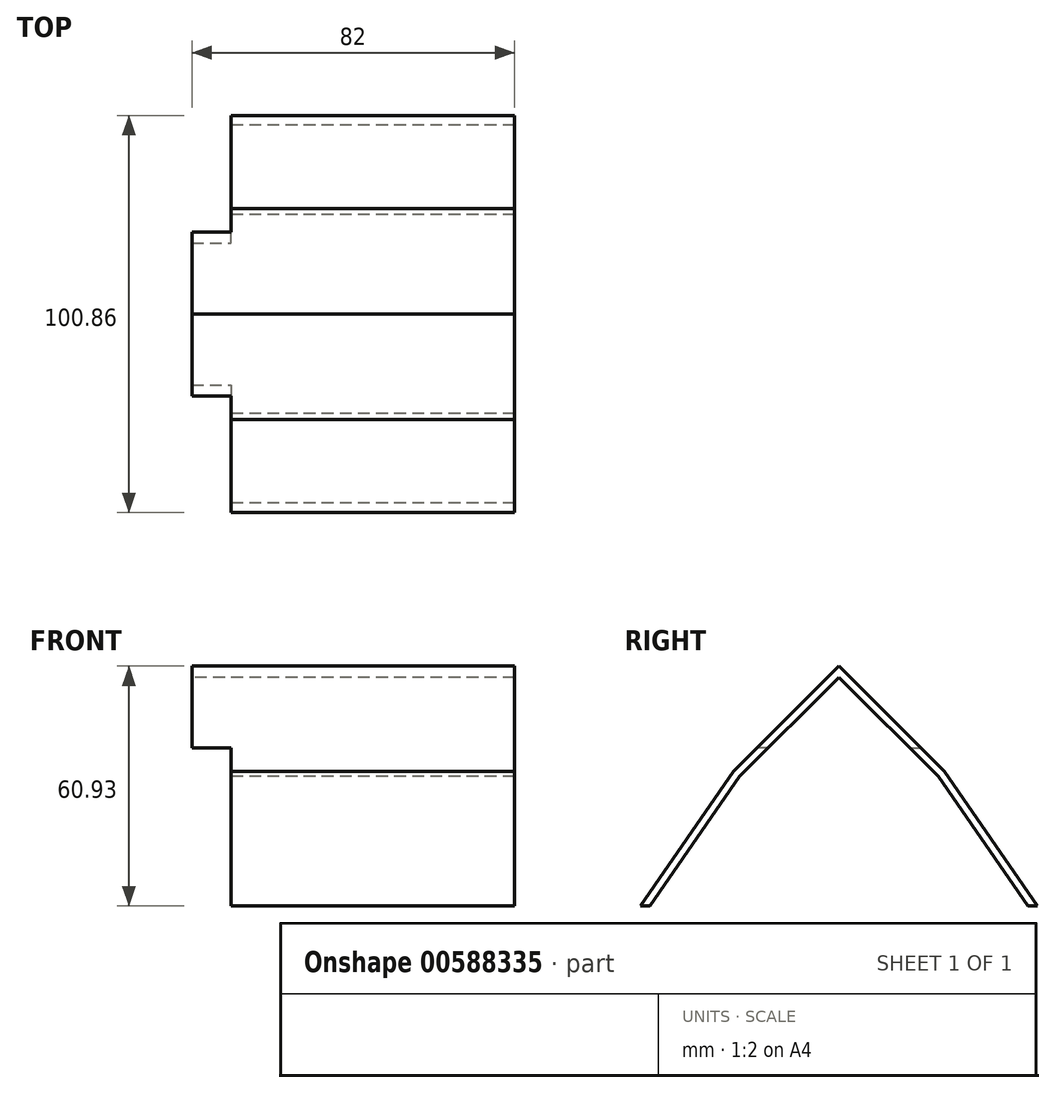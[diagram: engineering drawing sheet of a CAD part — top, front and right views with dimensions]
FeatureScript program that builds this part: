
annotation { "Feature Type Name" : "Feature", "Feature Type Description" : "" }
export const myFeature = defineFeature(function(context is Context, id is Id, definition is map)
    precondition{}
    {
        {
            var Q0;
            Q0=qCreatedBy(makeId("Right.planeOp"),FACE);
            var sketch = newSketch(context, id + "F0", { "sketchPlane" : qUnion([Q0])});
            skLineSegment(sketch, "E0", {"start": v(-88.43, 48.66) * mm, "end": v(-106.43, 30.66) * mm});
            skLineSegment(sketch, "E1", {"start": v(-88.43, 48.66) * mm, "end": v(-70.43, 30.66) * mm});
            skLineSegment(sketch, "E2", {"start": v(-70.43, 30.66) * mm, "end": v(-63.18, 23.42) * mm});
            skLineSegment(sketch, "E3", {"start": v(-113.68, 23.42) * mm, "end": v(-106.43, 30.66) * mm});
            skLineSegment(sketch, "E4", {"start": v(-40.43, -9.44) * mm, "end": v(-63.18, 23.42) * mm});
            skLineSegment(sketch, "E5", {"start": v(-136.43, -9.44) * mm, "end": v(-113.68, 23.42) * mm});
            skLineSegment(sketch, "E6", {"start": v(-136.43, -9.44) * mm, "end": v(-138.86, -9.44) * mm});
            skPoint(sketch, "E7.end.orphan", {"position": v(-143.24, -15.76) * mm});
            skPoint(sketch, "E7.start.orphan", {"position": v(-123.14, -15.76) * mm});
            skLineSegment(sketch, "E8", {"start": v(-40.43, -9.44) * mm, "end": v(-38, -9.44) * mm});
            skLineSegment(sketch, "E9", {"start": v(-61.65, 24.7) * mm, "end": v(-88.43, 51.5) * mm});
            skLineSegment(sketch, "E10", {"start": v(-61.65, 24.7) * mm, "end": v(-38, -9.44) * mm});
            skLineSegment(sketch, "E11", {"start": v(-88.43, 51.5) * mm, "end": v(-115.21, 24.7) * mm});
            skLineSegment(sketch, "E12", {"start": v(-115.21, 24.7) * mm, "end": v(-138.86, -9.44) * mm});
            skSolve(sketch);
        }
        {
            var Q0;
            Q0=makeQuery(id+"F0.imprint","IMPRINT",FACE,{"disambiguationData":[TD([[makeQuery(id+"F0.imprint","IMPRINT",EDGE,{"derivedFrom":sQuery(id+"F0.wireOp",EDGE,"E0")}),-1.0]])]});
            extrude(context, id + "F1", {"entities" : qUnion([Q0]), "depth" : 51 * mm, "offsetDistance" : 25 * mm});
        }
        {
            var Q0;
            Q0=makeQuery(id+"F1.opExtrude","CAP_FACE",FACE,{"disambiguationData":[OSD([sQuery(id+"F0.wireOp",EDGE,"E0"),sQuery(id+"F0.wireOp",EDGE,"E1"),sQuery(id+"F0.wireOp",EDGE,"E2"),sQuery(id+"F0.wireOp",EDGE,"E3"),sQuery(id+"F0.wireOp",EDGE,"E4"),sQuery(id+"F0.wireOp",EDGE,"E5"),sQuery(id+"F0.wireOp",EDGE,"E6"),sQuery(id+"F0.wireOp",EDGE,"E8"),sQuery(id+"F0.wireOp",EDGE,"E9"),sQuery(id+"F0.wireOp",EDGE,"E10"),sQuery(id+"F0.wireOp",EDGE,"E11"),sQuery(id+"F0.wireOp",EDGE,"E12")])],"isStart":false});
            extrude(context, id + "F2", {"entities" : qUnion([Q0]), "operationType" : NewBodyOperationType.REMOVE, "oppositeDirection" : true, "depth" : 2 * mm, "offsetDistance" : 25 * mm});
        }
        {
            var Q0;
            Q0=makeQuery(id+"F1.opExtrude","CAP_FACE",FACE,{"disambiguationData":[OSD([sQuery(id+"F0.wireOp",EDGE,"E0"),sQuery(id+"F0.wireOp",EDGE,"E1"),sQuery(id+"F0.wireOp",EDGE,"E2"),sQuery(id+"F0.wireOp",EDGE,"E3"),sQuery(id+"F0.wireOp",EDGE,"E4"),sQuery(id+"F0.wireOp",EDGE,"E5"),sQuery(id+"F0.wireOp",EDGE,"E6"),sQuery(id+"F0.wireOp",EDGE,"E8"),sQuery(id+"F0.wireOp",EDGE,"E9"),sQuery(id+"F0.wireOp",EDGE,"E10"),sQuery(id+"F0.wireOp",EDGE,"E11"),sQuery(id+"F0.wireOp",EDGE,"E12")])],"isStart":true});
            extrude(context, id + "F3", {"entities" : qUnion([Q0]), "operationType" : NewBodyOperationType.ADD, "depth" : 23 * mm, "offsetDistance" : 25 * mm});
        }
        {
            var Q0;
            Q0=makeQuery(id+"F3.opExtrude","CAP_FACE",FACE,{"disambiguationData":[OSD([sQuery(id+"F0.wireOp",EDGE,"E0"),sQuery(id+"F0.wireOp",EDGE,"E1"),sQuery(id+"F0.wireOp",EDGE,"E2"),sQuery(id+"F0.wireOp",EDGE,"E3"),sQuery(id+"F0.wireOp",EDGE,"E4"),sQuery(id+"F0.wireOp",EDGE,"E5"),sQuery(id+"F0.wireOp",EDGE,"E6"),sQuery(id+"F0.wireOp",EDGE,"E8"),sQuery(id+"F0.wireOp",EDGE,"E9"),sQuery(id+"F0.wireOp",EDGE,"E10"),sQuery(id+"F0.wireOp",EDGE,"E11"),sQuery(id+"F0.wireOp",EDGE,"E12")])],"isStart":false});
            var sketch = newSketch(context, id + "F4", { "sketchPlane" : qUnion([Q0])});
            skLineSegment(sketch, "E13.0", {"start": v(61.65, 24.7) * mm, "end": v(88.43, 51.5) * mm});
            skLineSegment(sketch, "E14.0", {"start": v(88.43, 48.66) * mm, "end": v(70.43, 30.66) * mm});
            skLineSegment(sketch, "E15.0", {"start": v(88.43, 48.66) * mm, "end": v(106.43, 30.66) * mm});
            skLineSegment(sketch, "E16.0", {"start": v(88.43, 51.5) * mm, "end": v(115.21, 24.7) * mm});
            skLineSegment(sketch, "E17", {"start": v(70.43, 30.66) * mm, "end": v(112.97, 30.66) * mm});
            skLineSegment(sketch, "E18", {"start": v(106.43, 30.66) * mm, "end": v(63.93, 30.66) * mm});
            skLineSegment(sketch, "E19", {"start": v(88.43, 51.5) * mm, "end": v(67.61, 30.66) * mm});
            skLineSegment(sketch, "E20", {"start": v(67.61, 30.66) * mm, "end": v(109.25, 30.66) * mm});
            skSolve(sketch);
        }
        {
            var Q0;
            {var subQ5=sQuery(id+"F4.wireOp",EDGE,"E14.0");Q0=makeQuery(id+"F4.imprint","IMPRINT",FACE,{"disambiguationData":[TD([[makeQuery(id+"F4.imprint","IMPRINT",EDGE,{"derivedFrom":subQ5}),-1.0]])]});}
            extrude(context, id + "F5", {"entities" : qUnion([Q0]), "operationType" : NewBodyOperationType.ADD, "depth" : 10 * mm, "offsetDistance" : 25 * mm});
        }
    });
